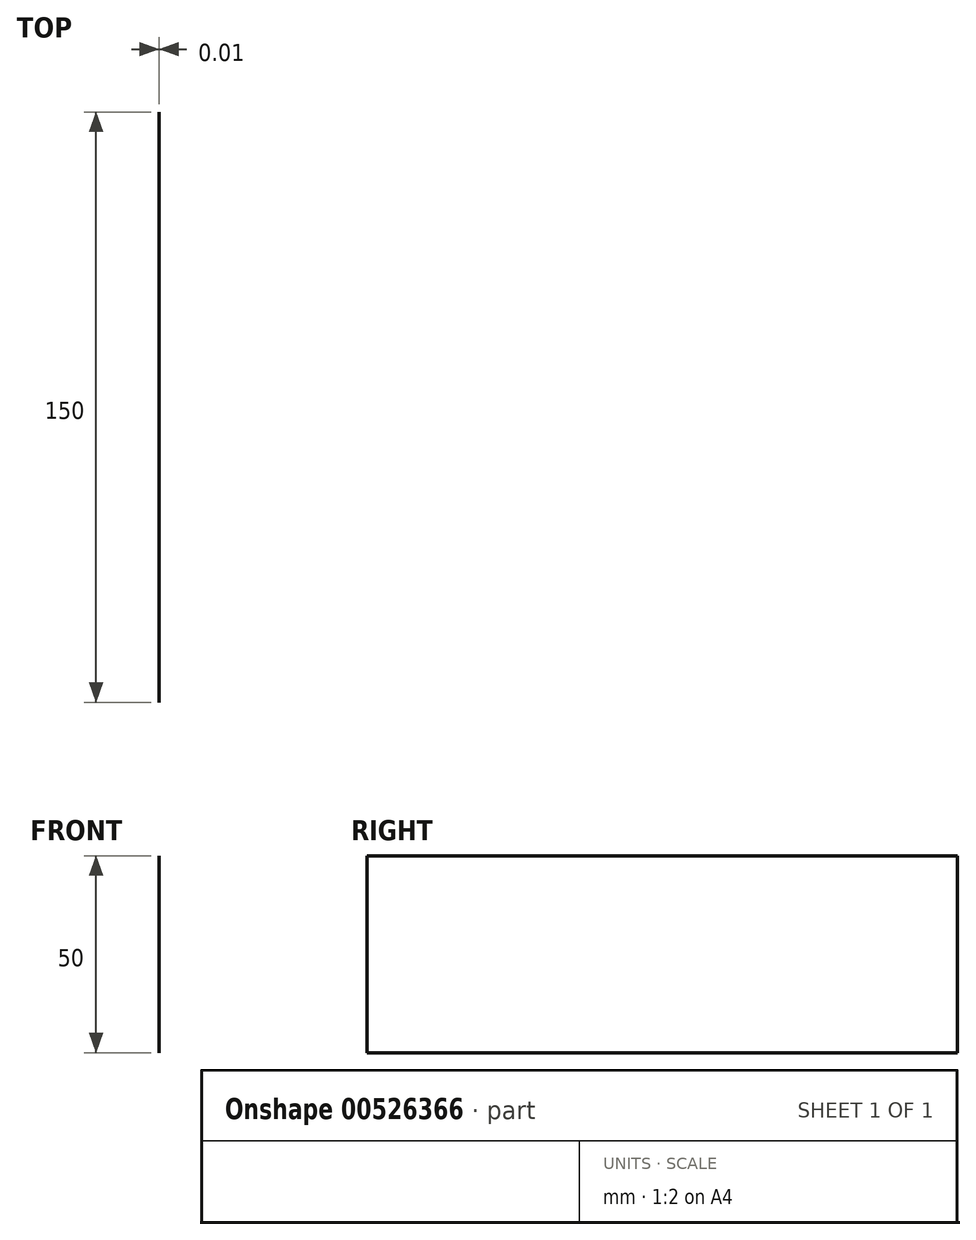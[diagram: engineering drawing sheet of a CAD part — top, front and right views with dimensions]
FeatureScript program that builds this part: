
annotation { "Feature Type Name" : "Feature", "Feature Type Description" : "" }
export const myFeature = defineFeature(function(context is Context, id is Id, definition is map)
    precondition{}
    {
        {
            var Q0;
            Q0=qCreatedBy(makeId("Right.planeOp"),FACE);
            var sketch = newSketch(context, id + "F0", { "sketchPlane" : qUnion([Q0])});
            skLineSegment(sketch, "E0.bottom", {"start": v(75, -25) * mm, "end": v(-75, -25) * mm});
            skLineSegment(sketch, "E0.top", {"start": v(75, 25) * mm, "end": v(-75, 25) * mm});
            skLineSegment(sketch, "E0.left", {"start": v(75, -25) * mm, "end": v(75, 25) * mm});
            skLineSegment(sketch, "E0.right", {"start": v(-75, -25) * mm, "end": v(-75, 25) * mm});
            skPoint(sketch, "E0.middle", {"position": v(0, 0) * mm});
            skSolve(sketch);
        }
        {
            var Q0;
            Q0 = qSketchRegion(id + "F0", true);
            extrude(context, id + "F1", {"entities" : qUnion([Q0]), "depth" : 0.01 * mm, "offsetDistance" : 25 * mm});
        }
    });
